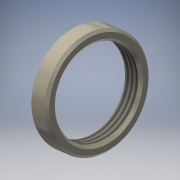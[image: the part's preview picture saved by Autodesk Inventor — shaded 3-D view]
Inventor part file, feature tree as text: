
AUTODESK INVENTOR PART (.ipt)
format: ipt  version: 2018 (Build 220112000, 112)  size: 126,464 bytes
history: native  units: mm
features: extrude x1, chamfer x1, thread x1, sketch x1
ambient origin geometry x8: Origin, YZ Plane, XZ Plane, XY Plane, X Axis, Y Axis, Z Axis, Center Point
bodies: Solid1 (feature_tree)
feature tree (4):
  extrude  "Extrusion1"  Depth=10.0mm
  chamfer  "Chamfer1"  Distance=2.0mm
  thread  "Thread1"  [1 undecoded]
  sketch  "Sketch1"  dims[d0=8.0mm d1=10.0mm d2=2.0mm d3=0.0mm d4=0.25mm d5=2.0mm d6=45.0deg d7=10.0mm d8=0.0mm]
note: 1 required parameter value undecoded (feature->parameter linkage not recoverable at this tier; creation-order binding heuristic only, values carry confidence <= 0.55)
